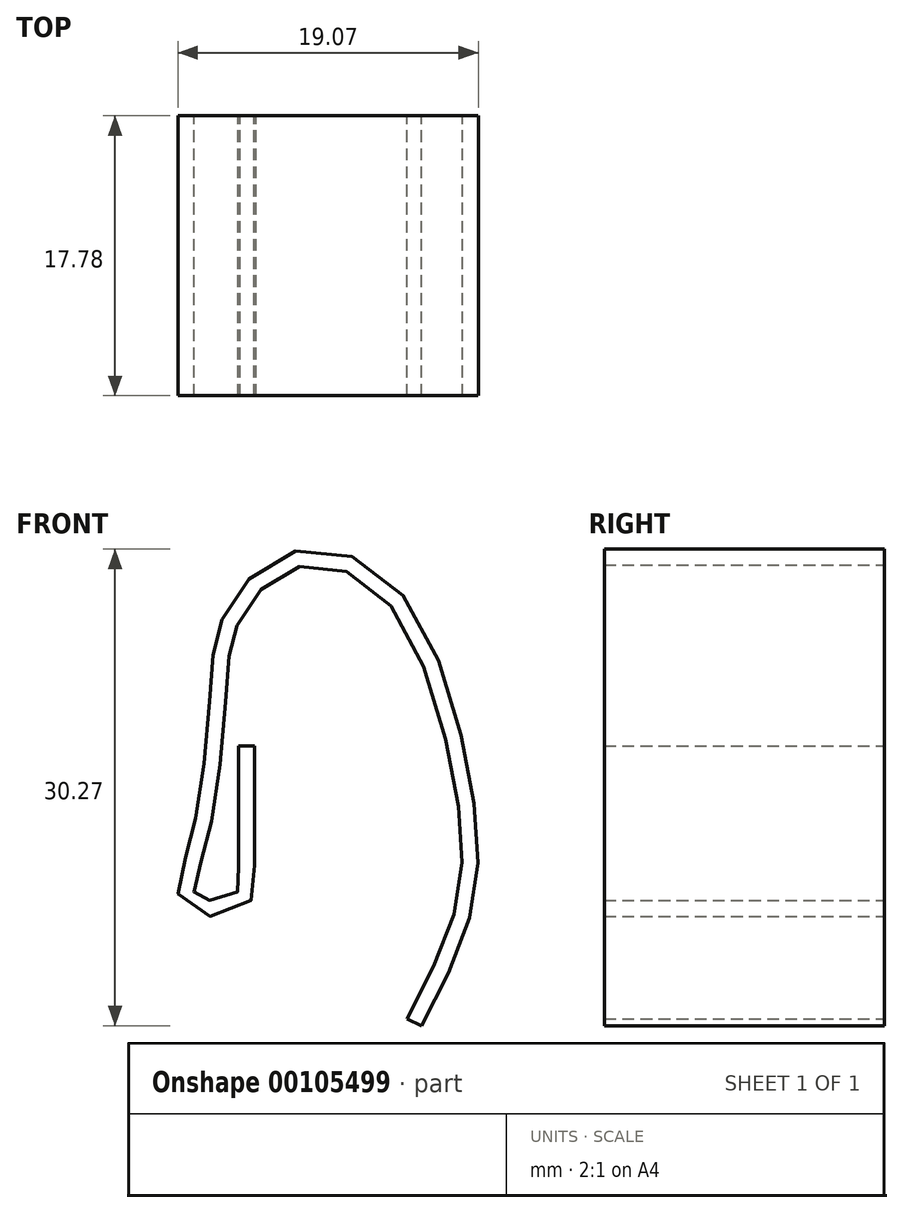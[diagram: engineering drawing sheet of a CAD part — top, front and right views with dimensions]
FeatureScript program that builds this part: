
annotation { "Feature Type Name" : "Feature", "Feature Type Description" : "" }
export const myFeature = defineFeature(function(context is Context, id is Id, definition is map)
    precondition{}
    {
        {
            var Q0;
            Q0=qCreatedBy(makeId("Front.planeOp"),FACE);
            var sketch = newSketch(context, id + "F0", { "sketchPlane" : qUnion([Q0])});
            skFitSpline(sketch, "E0", {"points": [v(0, 0) * mm, v(0, -5.08) * mm, v(0, -7.69) * mm, v(-0.33, -9.75) * mm, v(-3.52, -10) * mm, v(-3.6, -7.93) * mm, v(-2.58, -3.83) * mm, v(-1.7, 4.65) * mm, v(-1.16, 7.67) * mm, v(2.4, 11.6) * mm, v(8.82, 10.03) * mm, v(13.6, -1.78) * mm, v(13.87, -10.01) * mm, v(10.64, -17.55) * mm], "startDerivative": vector(-2.79, -82.1) * mm, "endDerivative": vector(-39.94, -75.17) * mm});
            skSolve(sketch);
        }
        {
            var Q0;
            Q0=qCreatedBy(makeId("Top.planeOp"),FACE);
            var sketch = newSketch(context, id + "F1", { "sketchPlane" : qUnion([Q0])});
            skLineSegment(sketch, "E1.bottom", {"start": v(0.5, -8.9) * mm, "end": v(-0.5, -8.9) * mm});
            skLineSegment(sketch, "E1.top", {"start": v(0.5, 8.9) * mm, "end": v(-0.5, 8.9) * mm});
            skLineSegment(sketch, "E1.left", {"start": v(0.5, -8.9) * mm, "end": v(0.5, 8.9) * mm});
            skLineSegment(sketch, "E1.right", {"start": v(-0.5, -8.9) * mm, "end": v(-0.5, 8.9) * mm});
            skPoint(sketch, "E1.middle", {"position": v(0, 0) * mm});
            skSolve(sketch);
        }
        {
            var Q0;
            Q0=makeQuery(id+"F1.imprint","IMPRINT",FACE,{"disambiguationData":[TD([[makeQuery(id+"F1.imprint","IMPRINT",EDGE,{"derivedFrom":sQuery(id+"F1.wireOp",EDGE,"E1.bottom")}),-1.0]])]});
            var Q1;
            Q1=sQuery(id+"F0.wireOp",EDGE,"E0");
            sweep(context, id + "F2", {"profiles" : qUnion([Q0]), "path" : qUnion([Q1])});
        }
    });
